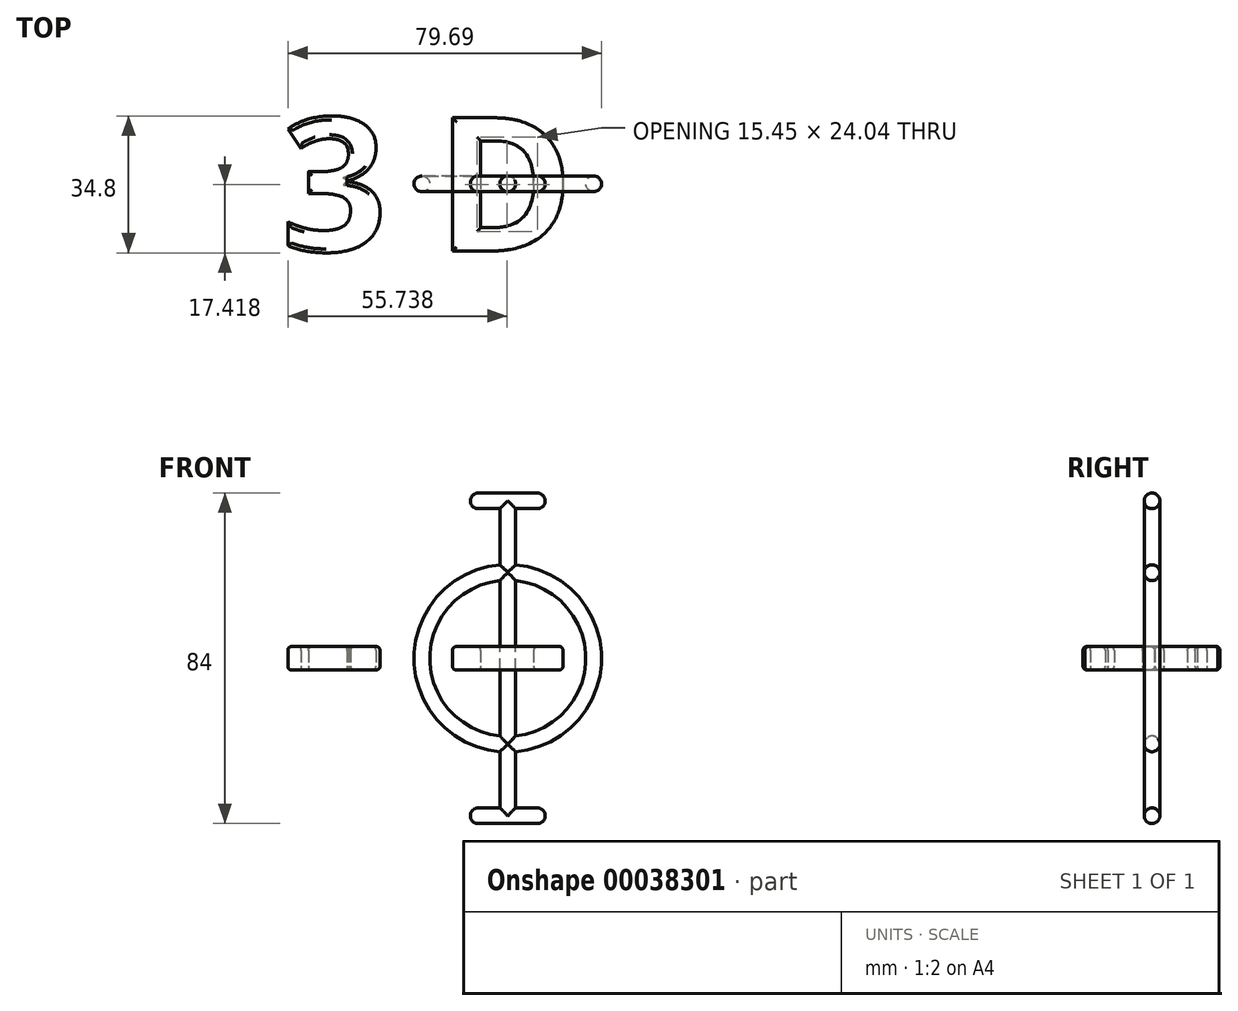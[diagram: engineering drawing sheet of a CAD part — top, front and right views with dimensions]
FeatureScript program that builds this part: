
annotation { "Feature Type Name" : "Feature", "Feature Type Description" : "" }
export const myFeature = defineFeature(function(context is Context, id is Id, definition is map)
    precondition{}
    {
        {
            var Q0;
            Q0=qCreatedBy(makeId("Top.planeOp"),FACE);
            var sketch = newSketch(context, id + "F0", { "sketchPlane" : qUnion([Q0])});
            skText(sketch, "E0", { "text": "3 D", "fontName": "OpenSans-Bold.ttf"});
            skPoint(sketch, "E1", {"position": v(0, 0) * mm});
            const initialGuessF0  = {"E0": [-0.03586, -0.01707, 1, 0, 0.03414]};
            skSetInitialGuess(sketch, initialGuessF0);
            skSolve(sketch);
        }
        {
            var Q0;
            Q0=makeQuery(id+"F0.imprint","IMPRINT",FACE,{"disambiguationData":[TD([[makeQuery(id+"F0.imprint","IMPRINT",EDGE,{"derivedFrom":sQuery(id+"F0.wireOp",EDGE,"E0.sketch_text.stroke-0")}),-1.0]])]});
            var Q1;
            Q1=makeQuery(id+"F0.imprint","IMPRINT",FACE,{"disambiguationData":[TD([[makeQuery(id+"F0.imprint","IMPRINT",EDGE,{"derivedFrom":sQuery(id+"F0.wireOp",EDGE,"1949aad5-839d-4fb3-a845-ca18cb88f10a.sketch_text.stroke-0")}),-1.0]])]});
            var Q2;
            Q2=makeQuery(id+"F0.imprint","IMPRINT",FACE,{"disambiguationData":[TD([[makeQuery(id+"F0.imprint","IMPRINT",EDGE,{"derivedFrom":sQuery(id+"F0.wireOp",EDGE,"1949aad5-839d-4fb3-a845-ca18cb88f10a.sketch_text.stroke-9")}),-1.0]])]});
            var Q3;
            Q3=makeQuery(id+"F0.imprint","IMPRINT",FACE,{"disambiguationData":[TD([[makeQuery(id+"F0.imprint","IMPRINT",EDGE,{"derivedFrom":sQuery(id+"F0.wireOp",EDGE,"1949aad5-839d-4fb3-a845-ca18cb88f10a.sketch_text.stroke-41")}),-1.0]])]});
            var Q4;
            Q4=makeQuery(id+"F0.imprint","IMPRINT",FACE,{"disambiguationData":[TD([[makeQuery(id+"F0.imprint","IMPRINT",EDGE,{"derivedFrom":sQuery(id+"F0.wireOp",EDGE,"E0.sketch_text.stroke-27")}),-1.0]])]});
            var Q5;
            Q5=makeQuery(id+"F0.imprint","IMPRINT",FACE,{"disambiguationData":[TD([[makeQuery(id+"F0.imprint","IMPRINT",EDGE,{"derivedFrom":sQuery(id+"F0.wireOp",EDGE,"1949aad5-839d-4fb3-a845-ca18cb88f10a.sketch_text.stroke-16")}),-1.0]])]});
            extrude(context, id + "F1", {"entities" : qUnion([Q0, Q1, Q2, Q3, Q4, Q5]), "endBound" : BoundingType.SYMMETRIC, "depth" : 6 * mm});
        }
        {
            var Q0;
            Q0=makeQuery(id+"F1.opExtrude","CAP_EDGE",EDGE,{"disambiguationData":[OSD([sQuery(id+"F0.wireOp",EDGE,"E0.sketch_text.stroke-6")])],"isStart":false});
            var Q1;
            Q1=makeQuery(id+"F1.opExtrude","CAP_EDGE",EDGE,{"disambiguationData":[OSD([sQuery(id+"F0.wireOp",EDGE,"E0.sketch_text.stroke-0")])],"isStart":false});
            var Q2;
            Q2=makeQuery(id+"F1.opExtrude","CAP_EDGE",EDGE,{"disambiguationData":[OSD([sQuery(id+"F0.wireOp",EDGE,"E0.sketch_text.stroke-23")])],"isStart":false});
            var Q3;
            Q3=makeQuery(id+"F1.opExtrude","CAP_EDGE",EDGE,{"disambiguationData":[OSD([sQuery(id+"F0.wireOp",EDGE,"E0.sketch_text.stroke-21")])],"isStart":false});
            var Q4;
            Q4=makeQuery(id+"F1.opExtrude","CAP_EDGE",EDGE,{"disambiguationData":[OSD([sQuery(id+"F0.wireOp",EDGE,"E0.sketch_text.stroke-16")])],"isStart":false});
            var Q5;
            Q5=makeQuery(id+"F1.opExtrude","CAP_EDGE",EDGE,{"disambiguationData":[OSD([sQuery(id+"F0.wireOp",EDGE,"E0.sketch_text.stroke-14")])],"isStart":false});
            var Q6;
            Q6=makeQuery(id+"F1.opExtrude","CAP_EDGE",EDGE,{"disambiguationData":[OSD([sQuery(id+"F0.wireOp",EDGE,"E0.sketch_text.stroke-8")])],"isStart":false});
            var Q7;
            Q7=makeQuery(id+"F1.opExtrude","CAP_EDGE",EDGE,{"disambiguationData":[OSD([sQuery(id+"F0.wireOp",EDGE,"E0.sketch_text.stroke-30")])],"isStart":false});
            var Q8;
            Q8=makeQuery(id+"F1.opExtrude","CAP_EDGE",EDGE,{"disambiguationData":[OSD([sQuery(id+"F0.wireOp",EDGE,"E0.sketch_text.stroke-31")])],"isStart":false});
            var Q9;
            Q9=makeQuery(id+"F1.opExtrude","CAP_EDGE",EDGE,{"disambiguationData":[OSD([sQuery(id+"F0.wireOp",EDGE,"E0.sketch_text.stroke-36")])],"isStart":false});
            var Q10;
            Q10=makeQuery(id+"F1.opExtrude","CAP_EDGE",EDGE,{"disambiguationData":[OSD([sQuery(id+"F0.wireOp",EDGE,"E0.sketch_text.stroke-35")])],"isStart":false});
            var Q11;
            Q11=makeQuery(id+"F1.opExtrude","CAP_FACE",FACE,{"disambiguationData":[OSD([sQuery(id+"F0.wireOp",EDGE,"E0.sketch_text.stroke-27"),sQuery(id+"F0.wireOp",EDGE,"E0.sketch_text.stroke-28"),sQuery(id+"F0.wireOp",EDGE,"E0.sketch_text.stroke-29"),sQuery(id+"F0.wireOp",EDGE,"E0.sketch_text.stroke-30"),sQuery(id+"F0.wireOp",EDGE,"E0.sketch_text.stroke-31"),sQuery(id+"F0.wireOp",EDGE,"E0.sketch_text.stroke-32"),sQuery(id+"F0.wireOp",EDGE,"E0.sketch_text.stroke-33"),sQuery(id+"F0.wireOp",EDGE,"E0.sketch_text.stroke-34"),sQuery(id+"F0.wireOp",EDGE,"E0.sketch_text.stroke-35"),sQuery(id+"F0.wireOp",EDGE,"E0.sketch_text.stroke-36"),sQuery(id+"F0.wireOp",EDGE,"E0.sketch_text.stroke-37"),sQuery(id+"F0.wireOp",EDGE,"E0.sketch_text.stroke-38")])],"isStart":true});
            var Q12;
            Q12=makeQuery(id+"F1.opExtrude","CAP_FACE",FACE,{"disambiguationData":[OSD([sQuery(id+"F0.wireOp",EDGE,"E0.sketch_text.stroke-0"),sQuery(id+"F0.wireOp",EDGE,"E0.sketch_text.stroke-1"),sQuery(id+"F0.wireOp",EDGE,"E0.sketch_text.stroke-2"),sQuery(id+"F0.wireOp",EDGE,"E0.sketch_text.stroke-3"),sQuery(id+"F0.wireOp",EDGE,"E0.sketch_text.stroke-4"),sQuery(id+"F0.wireOp",EDGE,"E0.sketch_text.stroke-5"),sQuery(id+"F0.wireOp",EDGE,"E0.sketch_text.stroke-6"),sQuery(id+"F0.wireOp",EDGE,"E0.sketch_text.stroke-7"),sQuery(id+"F0.wireOp",EDGE,"E0.sketch_text.stroke-8"),sQuery(id+"F0.wireOp",EDGE,"E0.sketch_text.stroke-9"),sQuery(id+"F0.wireOp",EDGE,"E0.sketch_text.stroke-10"),sQuery(id+"F0.wireOp",EDGE,"E0.sketch_text.stroke-11"),sQuery(id+"F0.wireOp",EDGE,"E0.sketch_text.stroke-12"),sQuery(id+"F0.wireOp",EDGE,"E0.sketch_text.stroke-13"),sQuery(id+"F0.wireOp",EDGE,"E0.sketch_text.stroke-14"),sQuery(id+"F0.wireOp",EDGE,"E0.sketch_text.stroke-15"),sQuery(id+"F0.wireOp",EDGE,"E0.sketch_text.stroke-16"),sQuery(id+"F0.wireOp",EDGE,"E0.sketch_text.stroke-17"),sQuery(id+"F0.wireOp",EDGE,"E0.sketch_text.stroke-18"),sQuery(id+"F0.wireOp",EDGE,"E0.sketch_text.stroke-19"),sQuery(id+"F0.wireOp",EDGE,"E0.sketch_text.stroke-20"),sQuery(id+"F0.wireOp",EDGE,"E0.sketch_text.stroke-21"),sQuery(id+"F0.wireOp",EDGE,"E0.sketch_text.stroke-22"),sQuery(id+"F0.wireOp",EDGE,"E0.sketch_text.stroke-23"),sQuery(id+"F0.wireOp",EDGE,"E0.sketch_text.stroke-24"),sQuery(id+"F0.wireOp",EDGE,"E0.sketch_text.stroke-25"),sQuery(id+"F0.wireOp",EDGE,"E0.sketch_text.stroke-26")])],"isStart":true});
            fillet(context, id + "F2", {"entities" : qUnion([Q0, Q1, Q2, Q3, Q4, Q5, Q6, Q7, Q8, Q9, Q10, Q11, Q12]), "radius" : 1 * mm, "tangentPropagation" : true, "allowEdgeOverflow" : false});
        }
        {
            var Q0;
            Q0=qCreatedBy(makeId("Top.planeOp"),FACE);
            var sketch = newSketch(context, id + "F3", { "sketchPlane" : qUnion([Q0])});
            skCircle(sketch, "E2", {"center": v(0, 0) * mm, "radius": 2 * mm});
            skSolve(sketch);
        }
        {
            var Q0;
            Q0=qCreatedBy(makeId("Top.planeOp"),FACE);
            var sketch = newSketch(context, id + "F4", { "sketchPlane" : qUnion([Q0])});
            skLineSegment(sketch, "E3", {"start": v(7.78, 0) * mm, "end": v(35.86, 0) * mm, "construction": true});
            skLineSegment(sketch, "E4", {"start": v(21.82, 0) * mm, "end": v(21.82, 25.8) * mm, "construction": true});
            skPoint(sketch, "E5", {"position": v(21.82, 0) * mm});
            skSolve(sketch);
        }
        {
            var Q0;
            Q0 = qSketchRegion(id + "F3", true);
            var Q1;
            Q1=sQuery(id+"F4.wireOp",EDGE,"E4");
            revolve(context, id + "F5", {"entities" : qUnion([Q0]), "axis" : qUnion([Q1]), "revolveType" : RevolveType.FULL});
        }
        {
            var Q0;
            Q0=qCreatedBy(makeId("Front.planeOp"),FACE);
            var sketch = newSketch(context, id + "F6", { "sketchPlane" : qUnion([Q0])});
            skLineSegment(sketch, "E6", {"start": v(21.82, 0) * mm, "end": v(21.82, -40) * mm});
            skLineSegment(sketch, "E7", {"start": v(14.32, -40) * mm, "end": v(29.32, -40) * mm});
            skSolve(sketch);
        }
        {
            var Q0;
            Q0=qCreatedBy(makeId("Top.planeOp"),FACE);
            var sketch = newSketch(context, id + "F7", { "sketchPlane" : qUnion([Q0])});
            skCircle(sketch, "E8", {"center": v(21.82, 0) * mm, "radius": 2 * mm});
            skSolve(sketch);
        }
        {
            var Q0;
            Q0=makeQuery(id+"F7.imprint","IMPRINT",FACE,{"disambiguationData":[TD([[makeQuery(id+"F7.imprint","IMPRINT",EDGE,{"derivedFrom":sQuery(id+"F7.wireOp",EDGE,"E8")}),1.0]])]});
            extrude(context, id + "F8", {"entities" : qUnion([Q0]), "oppositeDirection" : true, "depth" : 40 * mm});
        }
        {
            var Q0;
            Q0=sQuery(id+"F6.wireOp",VERTEX,"E7.end");
            var Q1;
            Q1=qCreatedBy(makeId("Right.planeOp"),FACE);
            cPlane(context, id + "F9", {"entities" : qUnion([Q0, Q1]), "cplaneType" : CPlaneType.PLANE_POINT, "offset" : 150 * mm, "width" : 150 * mm, "height" : 150 * mm});
        }
        {
            var Q0;
            Q0=qCreatedBy(id+"F9.planeOp",FACE);
            var sketch = newSketch(context, id + "F10", { "sketchPlane" : qUnion([Q0])});
            skCircle(sketch, "E9", {"center": v(0, -40) * mm, "radius": 2 * mm});
            skSolve(sketch);
        }
        {
            var Q0;
            Q0 = qSketchRegion(id + "F10", true);
            extrude(context, id + "F11", {"entities" : qUnion([Q0]), "operationType" : NewBodyOperationType.ADD, "oppositeDirection" : true, "depth" : 15 * mm});
        }
        {
            var Q0;
            Q0=makeQuery(id+"F11.opExtrude","CAP_FACE",FACE,{"disambiguationData":[OSD([sQuery(id+"F10.wireOp",EDGE,"E9")])],"isStart":true});
            var sketch = newSketch(context, id + "F12", { "sketchPlane" : qUnion([Q0])});
            skLineSegment(sketch, "E10", {"start": v(0, -42) * mm, "end": v(0, -38) * mm});
            skSolve(sketch);
        }
        {
            var Q0;
            {var subQ1=sQuery(id+"F12.wireOp",EDGE,"E10");Q0=makeQuery(id+"F12.imprint","IMPRINT",FACE,{"disambiguationData":[TD([[makeQuery(id+"F12.imprint","IMPRINT",EDGE,{"derivedFrom":subQ1}),-1.0]])]});}
            var Q1;
            Q1=sQuery(id+"F12.wireOp",EDGE,"E10");
            revolve(context, id + "F13", {"operationType" : NewBodyOperationType.ADD, "entities" : qUnion([Q0]), "axis" : qUnion([Q1]), "revolveType" : RevolveType.FULL});
        }
        {
            var Q0;
            Q0=makeQuery(id+"F11.opExtrude","CAP_FACE",FACE,{"disambiguationData":[OSD([sQuery(id+"F10.wireOp",EDGE,"E9")])],"isStart":false});
            var sketch = newSketch(context, id + "F14", { "sketchPlane" : qUnion([Q0])});
            skLineSegment(sketch, "E11", {"start": v(0, -38) * mm, "end": v(0, -42) * mm});
            skSolve(sketch);
        }
        {
            var Q0;
            {var subQ1=sQuery(id+"F14.wireOp",EDGE,"E11");Q0=makeQuery(id+"F14.imprint","IMPRINT",FACE,{"disambiguationData":[TD([[makeQuery(id+"F14.imprint","IMPRINT",EDGE,{"derivedFrom":subQ1}),-1.0]])]});}
            var Q1;
            Q1=sQuery(id+"F14.wireOp",EDGE,"E11");
            revolve(context, id + "F15", {"operationType" : NewBodyOperationType.ADD, "entities" : qUnion([Q0]), "axis" : qUnion([Q1]), "revolveType" : RevolveType.FULL});
        }
        {
            var Q0;
            Q0=makeQuery(id+"F8.opExtrude","SWEPT_BODY",BODY,{"disambiguationData":[OSD([sQuery(id+"F7.wireOp",EDGE,"E8")])]});
            var Q1;
            Q1=makeQuery(id+"F11.opExtrude","SWEPT_BODY",BODY,{"disambiguationData":[OSD([sQuery(id+"F10.wireOp",EDGE,"E9")])]});
            var Q2;
            Q2=makeQuery(id+"F13.opRevolve","SWEPT_BODY",BODY,{"disambiguationData":[OSD([sQuery(id+"F10.wireOp",EDGE,"E9"),sQuery(id+"F12.wireOp",EDGE,"E10")])]});
            var Q3;
            Q3=makeQuery(id+"F15.opRevolve","SWEPT_BODY",BODY,{"disambiguationData":[OSD([sQuery(id+"F10.wireOp",EDGE,"E9"),sQuery(id+"F14.wireOp",EDGE,"E11")])]});
            var Q4;
            Q4=qCreatedBy(makeId("Top.planeOp"),FACE);
            mirror(context, id + "F16", {"operationType" : NewBodyOperationType.ADD, "entities" : qUnion([Q0, Q1, Q2, Q3]), "mirrorPlane" : qUnion([Q4])});
        }
    });
